# Revit family: Drain_Wide_Flange_12_Inch-Zurn-Z532-Heavy-Duty
name_source: partatom
category: Plumbing Fixtures
units: mm (PartAtom-declared; Revit-internal decimal feet)

## family parameters
Always vertical = Yes
Cut with Voids When Loaded = No
Maintain Annotation Orientation = No
OmniClass Number = 23.70.50.21.24.14
OmniClass Title = Deck Waste Water Drains
Part Type = Normal
Room Calculation Point = No
Round Connector Dimension = Use Radius
Shared = No
Work Plane-Based = No

## types (18) — shared parameters
Approx. Weight (Lbs) = 54 "
Assembly Code = D2030300
CW Connection = No
Default Elevation = 25 "
Description = 12-1/4 [311] DIAMETER WIDE FLANGE HEAVY-DUTY FLOOR DRAIN
Frame Dimension = 2 "
Grate Open Area Sq.in = 30 "
HW Connection = No
Main Material = Iron - Zurn - Cast - Painted - Blue
Manufacturer = Zurn Water, LLC
Manufacurer Brand = Zurn
Modified Date = 12/19/2025
Product Documentation Link = https://files.zurn.com
Product Page URL = https://www.zurn.com
Product data url = https://www.bimobject.com
Top Diameter = 9 "
Top Diameter Inner = 12.25 "
Top Diameter Width = 20 "
URL = www.zurn.com
Vent Connection = No
WFU = 1
Waste Connection = Yes
ZN-TOP = No
zero-valued in all types: CWFU, HWFU

## per-type parameters (varying)
| type | A_ Pipe Size (Actual-Inner) | A_ Pipe Size (Actual-Outer) | A_ Pipe Size (Nominal) | Body Height_E | Connector Radius | Frame And Grate | Model | Type Comments |
| Z532-2NH | 2.067 " | 2.375 " | 2 " | 5.25 " | 1 " | Iron - Zurn - Cast - Painted - Blue | Z532 | Z532-2 Inch-No-Hub Outlet |
| Z532-2NL | 2.067 " | 2.375 " | 2 " | 4.5 " | 1 " | Iron - Zurn - Cast - Painted - Blue | Z532 | Z532-2 Inch-Neo-Loc Outlet |
| Z532-3IC | 3.068 " | 3.5 " | 3 " | 5.25 " | 1.5 " | Iron - Zurn - Cast - Painted - Blue | Z532 | Z532-3 Inch-Inside Caulk Outlet |
| Z532-3NH | 3.068 " | 3.5 " | 3 " | 5.25 " | 1.5 " | Iron - Zurn - Cast - Painted - Blue | Z532 | Z532-3 Inch-No-Hub Outlet |
| Z532-3NL | 3.068 " | 3.5 " | 3 " | 4.5 " | 1.5 " | Iron - Zurn - Cast - Painted - Blue | Z532 | Z532-3 Inch-Neo-Loc Outlet |
| Z532-4IC | 4.026 " | 4.5 " | 4 " | 5.25 " | 2 " | Iron - Zurn - Cast - Painted - Blue | Z532 | Z532-4 Inch-Inside Caulk Outlet |
| Z532-4NH | 4.026 " | 4.5 " | 4 " | 5.25 " | 2 " | Iron - Zurn - Cast - Painted - Blue | Z532 | Z532-4 Inch-No-Hub Outlet |
| Z532-4NL | 4.026 " | 4.5 " | 4 " | 4.5 " | 2 " | Iron - Zurn - Cast - Painted - Blue | Z532 | Z532-4 Inch-Neo-Loc Outlet |
| Z532-6NH | 6.065 " | 6.625 " | 6 " | 5.25 " | 3 " | Iron - Zurn - Cast - Painted - Blue | Z532 | Z532-6 Inch-No-Hub Outlet |
| ZN532-2NH | 2.067 " | 2.375 " | 2 " | 5.25 " | 1 " | Bronze - Zurn - Polished Nickel | ZN532 | ZN532-2 Inch-No-Hub Outlet |
| ZN532-2NL | 2.067 " | 2.375 " | 2 " | 4.5 " | 1 " | Bronze - Zurn - Polished Nickel | ZN532 | ZN532-2 Inch-Neo-Loc Outlet |
| ZN532-3IC | 3.068 " | 3.5 " | 3 " | 5.25 " | 1.5 " | Bronze - Zurn - Polished Nickel | ZN532 | ZN532-3 Inch-Inside Caulk Outlet |
| ZN532-3NH | 3.068 " | 3.5 " | 3 " | 5.25 " | 1.5 " | Bronze - Zurn - Polished Nickel | ZN532 | ZN532-3 Inch-No-Hub Outlet |
| ZN532-3NL | 3.068 " | 3.5 " | 3 " | 4.5 " | 1.5 " | Bronze - Zurn - Polished Nickel | ZN532 | ZN532-3 Inch-Neo-Loc Outlet |
| ZN532-4IC | 4.026 " | 4.5 " | 4 " | 5.25 " | 2 " | Bronze - Zurn - Polished Nickel | ZN532 | ZN532-4 Inch-Inside Caulk Outlet |
| ZN532-4NH | 4.026 " | 4.5 " | 4 " | 5.25 " | 2 " | Bronze - Zurn - Polished Nickel | ZN532 | ZN532-4 Inch-No-Hub Outlet |
| ZN532-4NL | 4.026 " | 4.5 " | 4 " | 4.5 " | 2 " | Bronze - Zurn - Polished Nickel | ZN532 | ZN532-4 Inch-Neo-Loc Outlet |
| ZN532-6NH | 6.065 " | 6.625 " | 6 " | 5.25 " | 3 " | Bronze - Zurn - Polished Nickel | ZN532 | ZN532-6 Inch-No-Hub Outlet |

## geometry (parser evidence)
native form markers: Sweep x4
no freeform markers — native parametric forms only
